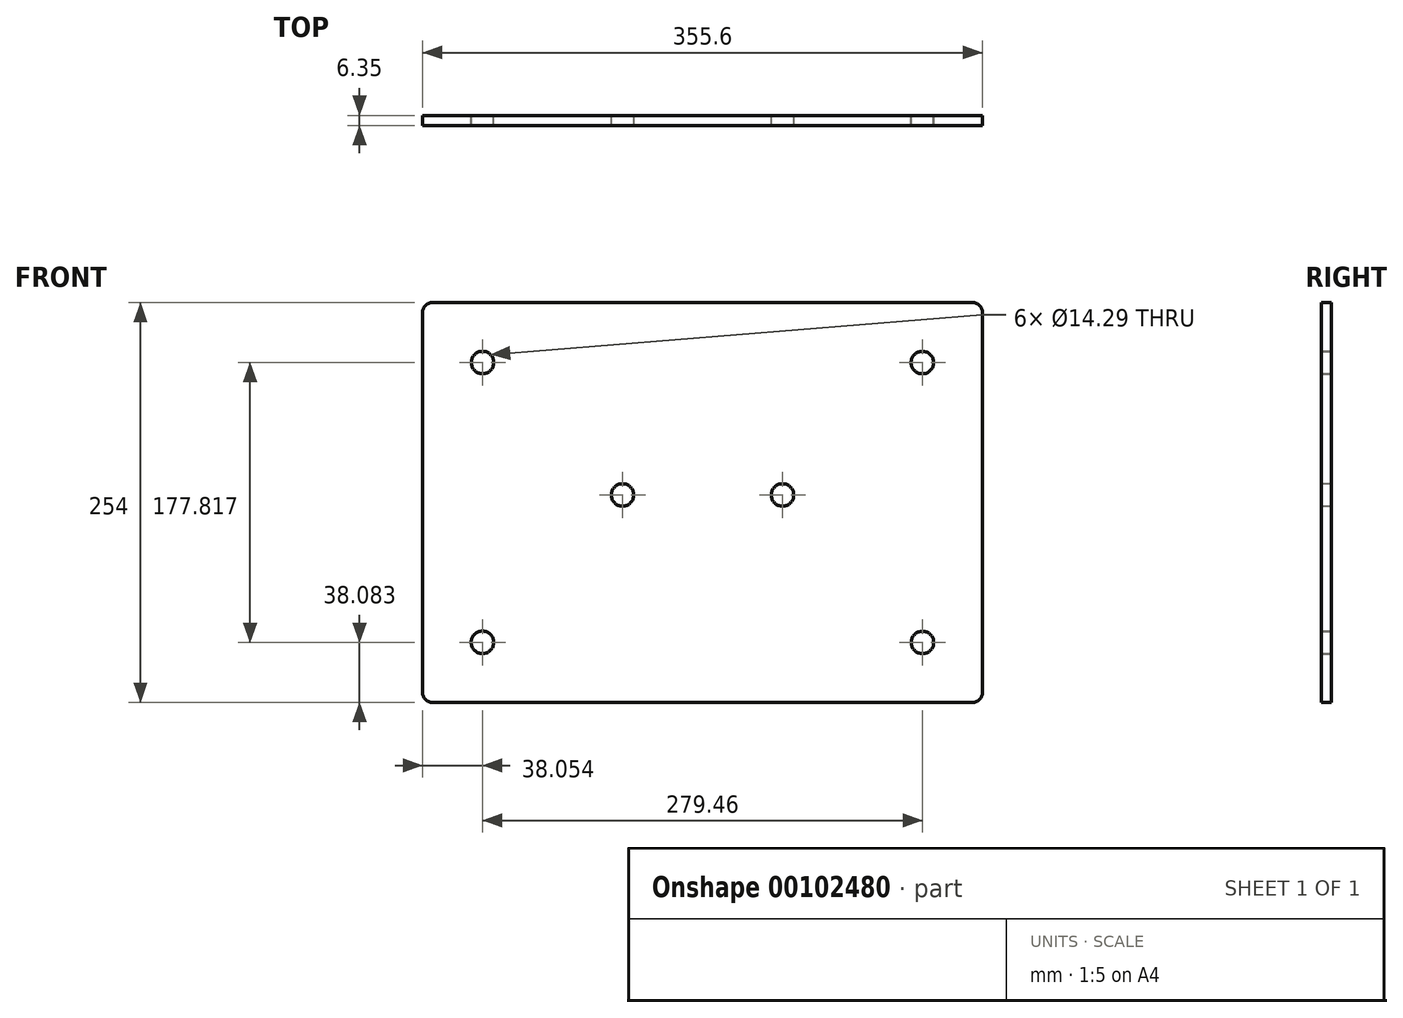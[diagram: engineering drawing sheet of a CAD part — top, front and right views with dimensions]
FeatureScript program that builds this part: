
annotation { "Feature Type Name" : "Feature", "Feature Type Description" : "" }
export const myFeature = defineFeature(function(context is Context, id is Id, definition is map)
    precondition{}
    {
        {
            var Q0;
            Q0=qCreatedBy(makeId("Front.planeOp"),FACE);
            var sketch = newSketch(context, id + "F0", { "sketchPlane" : qUnion([Q0])});
            skArc(sketch, "E0", {"start": v(-177.8, 120.65) * mm, "mid": v(-175.94, 125.14) * mm, "end": v(-171.45, 127) * mm});
            skLineSegment(sketch, "E1", {"start": v(-171.45, 127) * mm, "end": v(171.45, 127) * mm});
            skArc(sketch, "E2", {"start": v(171.45, 127) * mm, "mid": v(175.94, 125.14) * mm, "end": v(177.8, 120.65) * mm});
            skLineSegment(sketch, "E3", {"start": v(177.8, 120.65) * mm, "end": v(177.8, -120.65) * mm});
            skArc(sketch, "E4", {"start": v(177.8, -120.65) * mm, "mid": v(175.94, -125.14) * mm, "end": v(171.45, -127) * mm});
            skLineSegment(sketch, "E5", {"start": v(171.45, -127) * mm, "end": v(-171.45, -127) * mm});
            skArc(sketch, "E6", {"start": v(-171.45, -127) * mm, "mid": v(-175.94, -125.14) * mm, "end": v(-177.8, -120.65) * mm});
            skLineSegment(sketch, "E7", {"start": v(-177.8, -120.65) * mm, "end": v(-177.8, 120.65) * mm});
            skLineSegment(sketch, "E8", {"start": v(177.8, -20.64) * mm, "end": v(177.8, -30.16) * mm});
            skLineSegment(sketch, "E9", {"start": v(-177.8, -30.16) * mm, "end": v(-177.8, -20.64) * mm});
            skCircle(sketch, "E10", {"center": v(-139.7, 88.9) * mm, "radius": 7.14 * mm});
            skCircle(sketch, "E11", {"center": v(139.65, 88.86) * mm, "radius": 7.14 * mm});
            skCircle(sketch, "E12", {"center": v(-50.8, 4.78) * mm, "radius": 7.14 * mm});
            skCircle(sketch, "E13", {"center": v(50.81, 4.76) * mm, "radius": 7.14 * mm});
            skCircle(sketch, "E14", {"center": v(-139.75, -88.85) * mm, "radius": 7.14 * mm});
            skCircle(sketch, "E15", {"center": v(139.71, -88.92) * mm, "radius": 7.14 * mm});
            skSolve(sketch);
        }
        {
            var Q0;
            Q0 = qSketchRegion(id + "F0", true);
            extrude(context, id + "F1", {"entities" : qUnion([Q0]), "depth" : 6.35 * mm});
        }
    });
